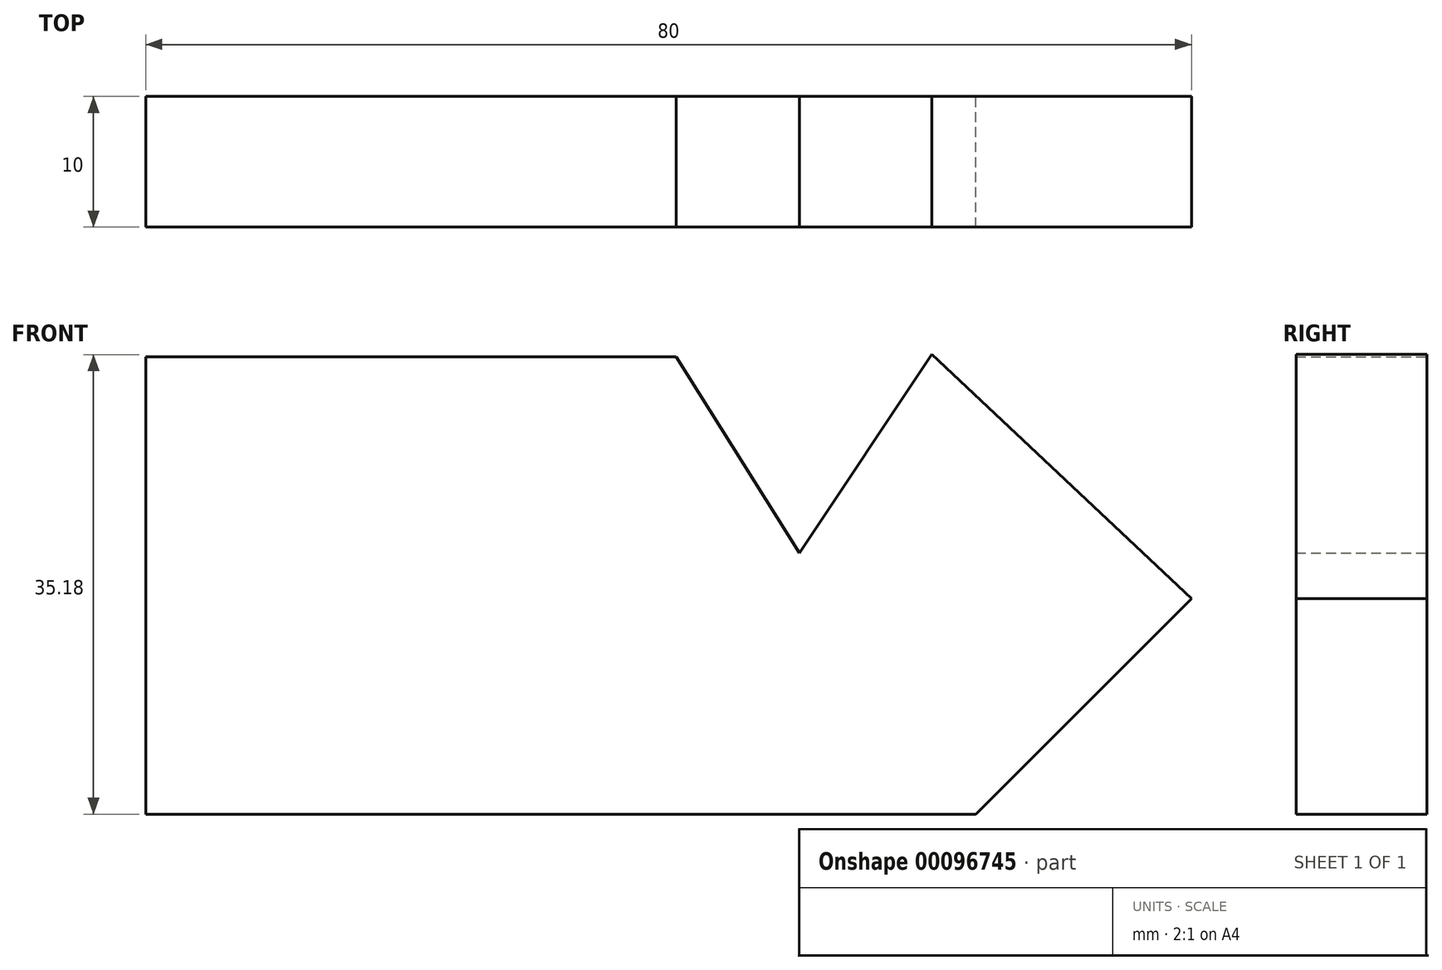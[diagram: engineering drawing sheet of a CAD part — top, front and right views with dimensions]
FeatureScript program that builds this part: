
annotation { "Feature Type Name" : "Feature", "Feature Type Description" : "" }
export const myFeature = defineFeature(function(context is Context, id is Id, definition is map)
    precondition{}
    {
        {
            var Q0;
            Q0=qCreatedBy(makeId("Front.planeOp"),FACE);
            var sketch = newSketch(context, id + "F0", { "sketchPlane" : qUnion([Q0])});
            skLineSegment(sketch, "E0", {"start": v(0, 0) * mm, "end": v(0, 35) * mm});
            skLineSegment(sketch, "E1", {"start": v(0, 35) * mm, "end": v(40.57, 35) * mm});
            skLineSegment(sketch, "E2", {"start": v(40.57, 35) * mm, "end": v(50, 20) * mm});
            skLineSegment(sketch, "E3", {"start": v(0, 0) * mm, "end": v(63.5, 0) * mm});
            skLineSegment(sketch, "E4", {"start": v(63.5, 0) * mm, "end": v(80, 16.5) * mm});
            skLineSegment(sketch, "E5", {"start": v(50, 20) * mm, "end": v(60.14, 35.18) * mm});
            skLineSegment(sketch, "E6", {"start": v(80, 16.5) * mm, "end": v(60.14, 35.18) * mm});
            skSolve(sketch);
        }
        {
            var Q0;
            Q0=makeQuery(id+"F0.imprint","IMPRINT",FACE,{"disambiguationData":[TD([[makeQuery(id+"F0.imprint","IMPRINT",EDGE,{"derivedFrom":sQuery(id+"F0.wireOp",EDGE,"E0")}),-1.0]])]});
            extrude(context, id + "F1", {"entities" : qUnion([Q0]), "depth" : 10 * mm});
        }
    });
